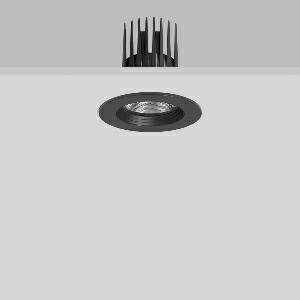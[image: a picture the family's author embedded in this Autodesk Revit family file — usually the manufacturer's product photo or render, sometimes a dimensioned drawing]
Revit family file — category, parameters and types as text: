
# Revit family: heledon_mini_e_901740_003_1_fd15
name_source: partatom
category: Lighting Fixtures
units: mm (PartAtom-declared; Revit-internal decimal feet)

## family parameters
Cut with Voids When Loaded = No
Host = Face
Light Source = No
Part Type = Normal
Room Calculation Point = No
Round Connector Dimension = Use Diameter
Shared = No

## types (1)
- HELEDON mini E (1 x LED Modul 940, 2700 lm, 4000)
    Apparent Load = 20 VA
    Approval mark = CE
    CIE Flux Codes = 100 100 100 100 100
    Color Rendering = 92
    Color Temperature = 4000
    Default Elevation = 1800 mm
    Description = Series: HELEDON mini
Round recessed downlight. Housing: die-cast aluminium, powder-coated. Black plastic ring and recessed LED to prevent glare from the side. Optical assembly with reflector made of MIRO-Silver with 98% total light reflection for outstanding efficiency - can be changed without tools. Best colour rendering index Ra>90. Suitable for Recessed ceiling mounting. Installation without tools thanks to spring fastening system. Including separate LED converter with connecting cable 600 mm.High quality converter without flickering and stroboscopic effect. Through-wiring box (5 pole) available as accessory. The following accessories can be mounted without use of tools: interchangeable lenses, decorative glasses, honeycomb louvre, clear and frosted diffusers, white interchangeable plastic ring. 
Colour: deep black, matt (RAL 9005)
Diameter: 124 mm
Height: 3 mm
Cut-out diameter: 114 mm
Recess height: 170 mm
Luminaire: recess height: 120 mm
Lamp: LED
Socket: without socket
Colour temperature: 4000K
Colour rendering index (CRI): 92
System power: 20 W
Rated luminous flux: 2700 lm
Luminous efficiency: 135 lm/W
Control gear: Regulated power supply
Protection class: II
Type of protection: IP 20
    Height = 0 mm  [stored 0 ft]
    Lamp = 1 x LED Modul 940
    Lamp Light Flux = 2700 lm
    Lamp count = 1
    Length = 124 mm  [stored 0.406824 ft]
    Lifetime = 50000 h
    Luminous efficacy = 135 lm/W
    Manufacturer = RZB
    ModVariant = No
    Model = 901740.003.1
    Mounting Place = Ceiling
    Mounting Type = Recessed
    Number of Poles = 1
    OnlyDefault = Yes
    Power Factor = 1
    Product Name = HELEDON mini E
    Product group = Recessed downlights
    ProductGroupID = 402
    Protection Class = Protection class II
    Protection Degree = IP 20
    RLX_Detail_Level = 1
    RLX_Emergency_Light_Flux = 0 lm
    RLX_Emergency_Type = 0
    RLX_Emergency_Type_DB = No
    RlxData = <blob elided: 127949 chars, md5=c98fa9c8>
    Socket = socket
    Standby Power = 0 W
    System Light Flux = 2700 lm
    System Power = 20 W
    Type Comments = Product without accessories
    Type Image = 901657.003.jpg
    URL = http://relux.com
    VarID = ---
    Voltage = 230 V
    Voltage Range = 220-240 V
    Weight = 0.00 kg
    Width = 0 mm  [stored 0 ft]

note: [stored X ft] marks values corroborated as IEEE doubles in the binary element streams (Revit-internal decimal feet)

## geometry (parser evidence)
native form markers: Blend x4, Sweep x12
no freeform markers — native parametric forms only
